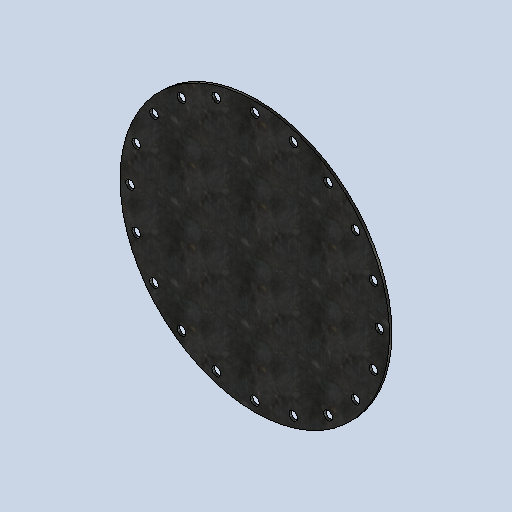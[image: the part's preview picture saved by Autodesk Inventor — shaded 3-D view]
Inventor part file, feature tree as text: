
AUTODESK INVENTOR PART (.ipt)
format: ipt  version: 2025.1 (Build 291241020, 241B)  size: 257,024 bytes
history: native  units: mm
features: sketch x2, other x2, extrude x1, pattern_circular x1
ambient origin geometry x8: Origin, YZ Plane, XZ Plane, XY Plane, X Axis, Y Axis, Z Axis, Center Point
bodies: Solid1 (feature_tree)
feature tree (6):
  extrude  "Extrusion1"  Depth=6.0mm TaperAngle=0.0deg
  pattern_circular  "Circular Pattern1"  Count=62  [1 undecoded]
  sketch  "Sketch1"  dims[d0=670.0mm d1=6.0mm d2=0.0mm]
  sketch  "Sketch2"  dims[d3=22.0mm d4=620.0mm d5=6.0mm d6=6.0mm d7=0.0mm d8=200.0mm d9=360.0deg]
  other  "Cut1"
  other  "Definition1"
note: 1 required parameter value undecoded (feature->parameter linkage not recoverable at this tier; creation-order binding heuristic only, values carry confidence <= 0.55)
